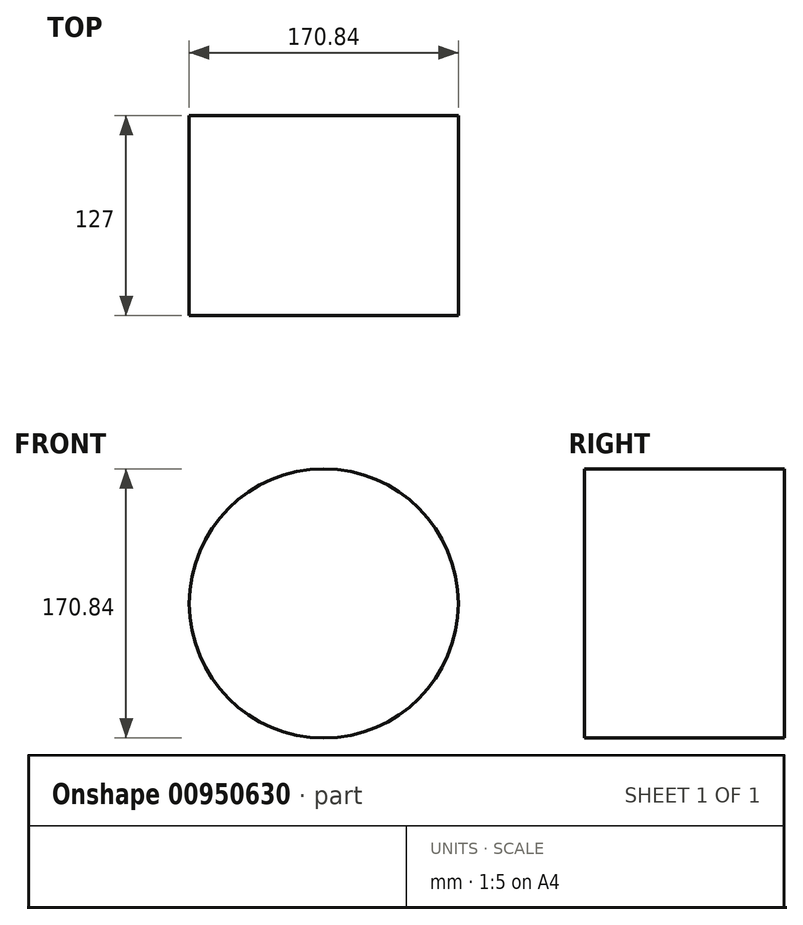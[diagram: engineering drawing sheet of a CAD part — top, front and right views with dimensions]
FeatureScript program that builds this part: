
annotation { "Feature Type Name" : "Feature", "Feature Type Description" : "" }
export const myFeature = defineFeature(function(context is Context, id is Id, definition is map)
    precondition{}
    {
        {
            var Q0;
            Q0=qCreatedBy(makeId("Front.planeOp"),FACE);
            var sketch = newSketch(context, id + "F0", { "sketchPlane" : qUnion([Q0])});
            skCircle(sketch, "E0", {"center": v(0, 0) * mm, "radius": 85.42 * mm});
            skSolve(sketch);
        }
        {
            var Q0;
            Q0 = qSketchRegion(id + "F0", true);
            extrude(context, id + "F1", {"entities" : qUnion([Q0]), "depth" : 127 * mm, "offsetDistance" : 25.4 * mm});
        }
    });
